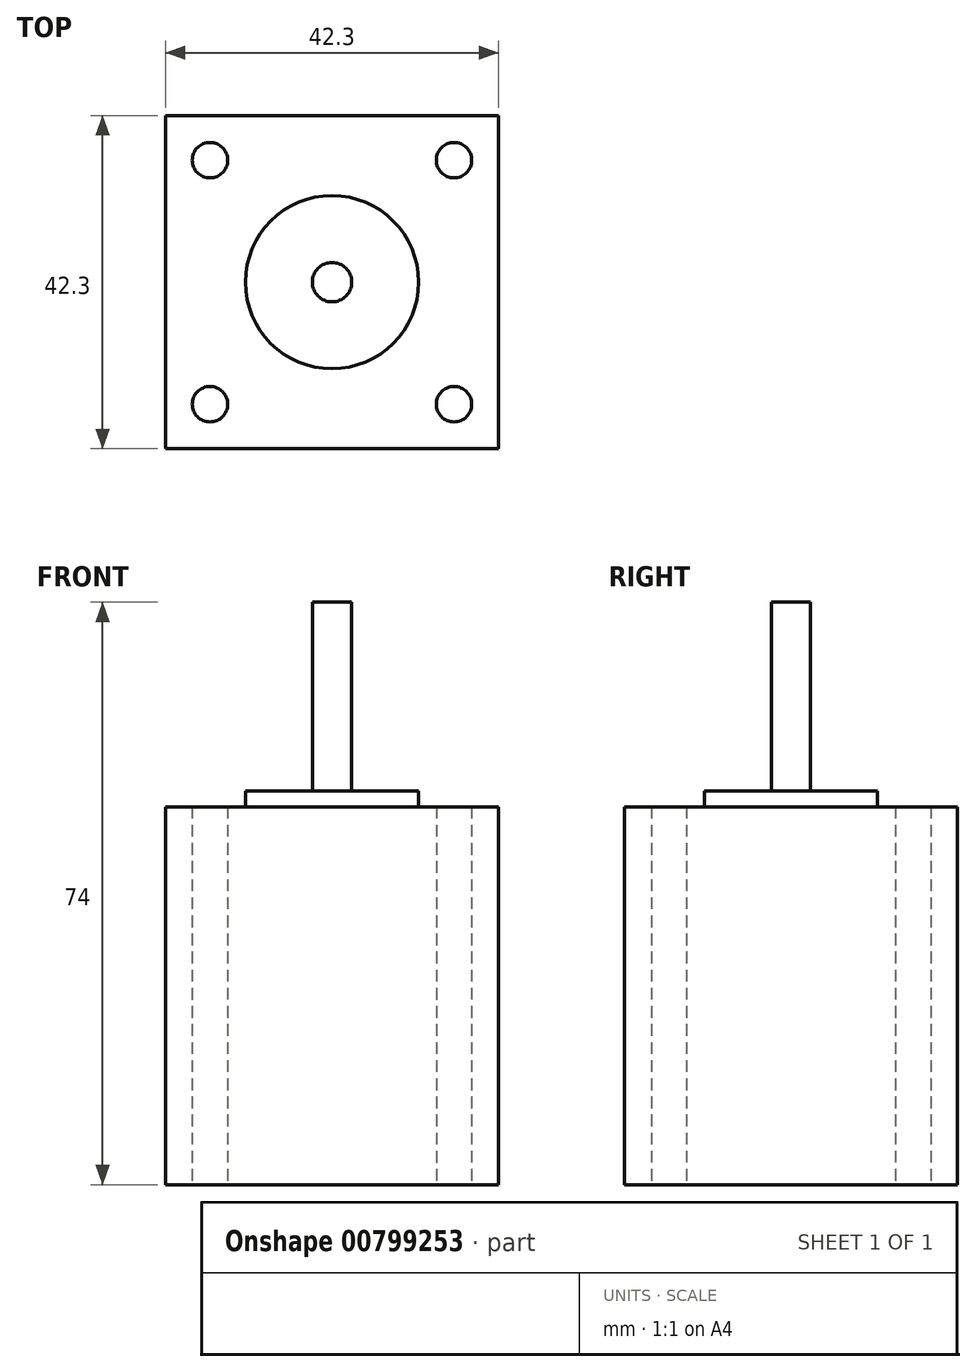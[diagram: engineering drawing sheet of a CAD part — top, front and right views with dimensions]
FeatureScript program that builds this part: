
annotation { "Feature Type Name" : "Feature", "Feature Type Description" : "" }
export const myFeature = defineFeature(function(context is Context, id is Id, definition is map)
    precondition{}
    {
        {
            assignVariable(context, id + "F0", {"name" : "shaft_length", "anyValue" : 24});
        }
        {
            assignVariable(context, id + "F1", {"name" : "hole_diameter", "anyValue" : 4.5});
        }
        {
            assignVariable(context, id + "F2", {"name" : "shaft_hump_depth", "anyValue" : 2});
        }
        {
            assignVariable(context, id + "F3", {"name" : "stepper_depth", "anyValue" : 48});
        }
        {
            var Q0;
            Q0=qCreatedBy(makeId("Top.planeOp"),FACE);
            var sketch = newSketch(context, id + "F4", { "sketchPlane" : qUnion([Q0])});
            skLineSegment(sketch, "E0.bottom", {"start": v(21.15, -21.15) * mm, "end": v(-21.15, -21.15) * mm});
            skLineSegment(sketch, "E0.top", {"start": v(21.15, 21.15) * mm, "end": v(-21.15, 21.15) * mm});
            skLineSegment(sketch, "E0.left", {"start": v(21.15, -21.15) * mm, "end": v(21.15, 21.15) * mm});
            skLineSegment(sketch, "E0.right", {"start": v(-21.15, -21.15) * mm, "end": v(-21.15, 21.15) * mm});
            skPoint(sketch, "E0.middle", {"position": v(0, 0) * mm});
            skLineSegment(sketch, "E1.bottom", {"start": v(15.5, -15.5) * mm, "end": v(-15.5, -15.5) * mm, "construction": true});
            skLineSegment(sketch, "E1.top", {"start": v(15.5, 15.5) * mm, "end": v(-15.5, 15.5) * mm, "construction": true});
            skLineSegment(sketch, "E1.left", {"start": v(15.5, -15.5) * mm, "end": v(15.5, 15.5) * mm, "construction": true});
            skLineSegment(sketch, "E1.right", {"start": v(-15.5, -15.5) * mm, "end": v(-15.5, 15.5) * mm, "construction": true});
            skCircle(sketch, "E2", {"center": v(0, 0) * mm, "radius": 11 * mm});
            skCircle(sketch, "E3", {"center": v(0, 0) * mm, "radius": 2.5 * mm});
            skSolve(sketch);
        }
        {
            var Q0;
            Q0=makeQuery(id+"F4.imprint","IMPRINT",FACE,{"disambiguationData":[TD([[makeQuery(id+"F4.imprint","IMPRINT",EDGE,{"derivedFrom":sQuery(id+"F4.wireOp",EDGE,"E0.bottom")}),-1.0]])]});
            extrude(context, id + "F5", {"entities" : qUnion([Q0]), "depth" : (getVariable(context, 'stepper_depth')) * mm, "offsetDistance" : 25 * mm});
        }
        {
            var Q0;
            Q0=makeQuery(id+"F4.imprint","IMPRINT",FACE,{"disambiguationData":[TD([[makeQuery(id+"F4.imprint","IMPRINT",EDGE,{"derivedFrom":sQuery(id+"F4.wireOp",EDGE,"E2")}),1.0]])]});
            extrude(context, id + "F6", {"entities" : qUnion([Q0]), "operationType" : NewBodyOperationType.ADD, "depth" : (getVariable(context, 'stepper_depth') + getVariable(context, 'shaft_hump_depth')) * mm, "offsetDistance" : 25 * mm});
        }
        {
            var Q0;
            Q0=makeQuery(id+"F4.imprint","IMPRINT",FACE,{"disambiguationData":[TD([[makeQuery(id+"F4.imprint","IMPRINT",EDGE,{"derivedFrom":sQuery(id+"F4.wireOp",EDGE,"E3")}),1.0]])]});
            extrude(context, id + "F7", {"entities" : qUnion([Q0]), "operationType" : NewBodyOperationType.ADD, "depth" : (getVariable(context, 'stepper_depth') + getVariable(context, 'shaft_hump_depth') + getVariable(context, 'shaft_length')) * mm, "offsetDistance" : 25 * mm});
        }
        {
            var Q0;
            Q0=sQuery(id+"F4.wireOp",VERTEX,"E1.top.start");
            var Q1;
            Q1=sQuery(id+"F4.wireOp",VERTEX,"E1.top.end");
            var Q2;
            Q2=sQuery(id+"F4.wireOp",VERTEX,"E1.bottom.end");
            var Q3;
            Q3=sQuery(id+"F4.wireOp",VERTEX,"E1.bottom.start");
            var Q4;
            Q4=makeQuery(id+"F5.opExtrude","SWEPT_BODY",BODY,{"disambiguationData":[OSD([sQuery(id+"F4.wireOp",EDGE,"E0.bottom"),sQuery(id+"F4.wireOp",EDGE,"E0.top"),sQuery(id+"F4.wireOp",EDGE,"E0.left"),sQuery(id+"F4.wireOp",EDGE,"E0.right"),sQuery(id+"F4.wireOp",EDGE,"E2")])]});
            hole(context, id + "F8", {"style" : HoleStyle.SIMPLE, "endStyle" : HoleEndStyle.BLIND, "oppositeDirection" : true, "holeDiameter" : (getVariable(context, 'hole_diameter')) * mm, "majorDiameter" : 5 * mm, "holeDepth" : (getVariable(context, 'stepper_depth')) * mm, "isTappedThrough" : true, "tappedDepth" : 12 * mm, "tapClearance" : 3, "startFromSketch" : true, "locations" : qUnion([Q0, Q1, Q2, Q3]), "scope" : qUnion([Q4])});
        }
    });
